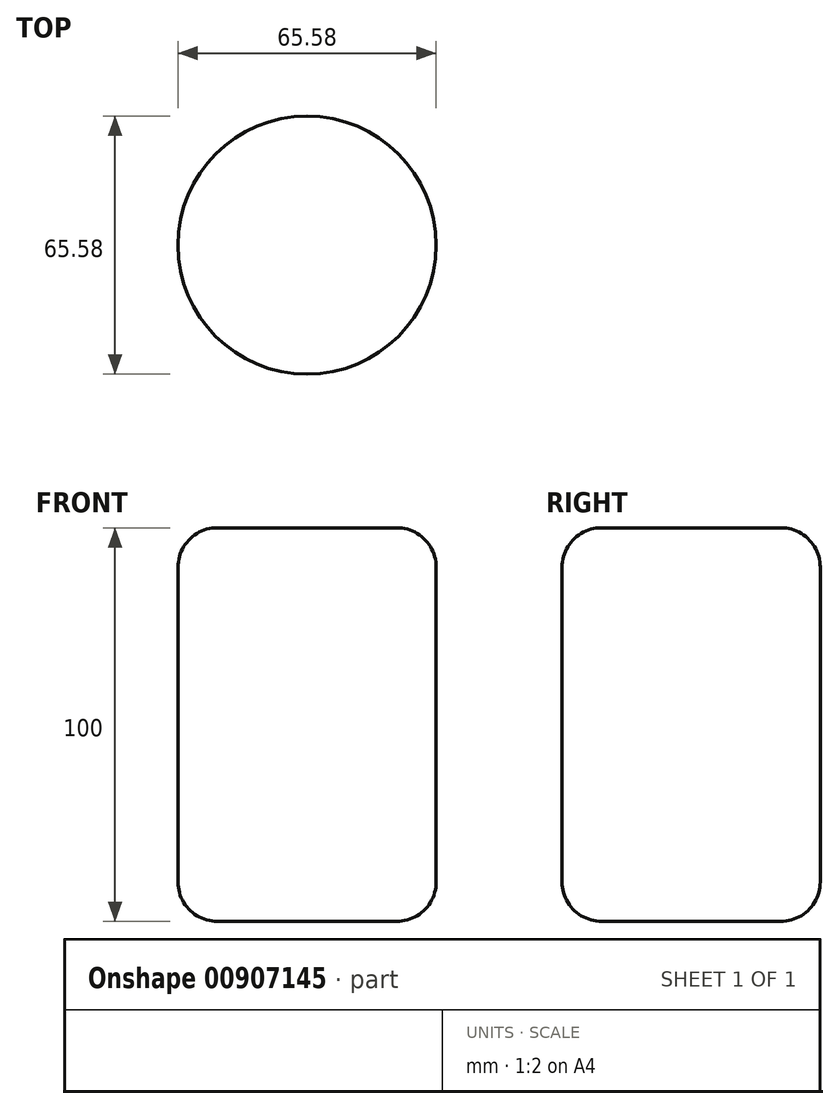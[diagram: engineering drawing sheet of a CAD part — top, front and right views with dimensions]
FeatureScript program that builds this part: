
annotation { "Feature Type Name" : "Feature", "Feature Type Description" : "" }
export const myFeature = defineFeature(function(context is Context, id is Id, definition is map)
    precondition{}
    {
        {
            var Q0;
            Q0=qCreatedBy(makeId("Top.planeOp"),FACE);
            var sketch = newSketch(context, id + "F0", { "sketchPlane" : qUnion([Q0])});
            skCircle(sketch, "E0", {"center": v(0, 0) * mm, "radius": 32.79 * mm});
            skSolve(sketch);
        }
        {
            var Q0;
            Q0 = qSketchRegion(id + "F0", true);
            extrude(context, id + "F1", {"entities" : qUnion([Q0]), "depth" : 100 * mm, "offsetDistance" : 25.4 * mm});
        }
        {
            var Q0;
            Q0=makeQuery(id+"F1.opExtrude","CAP_EDGE",EDGE,{"disambiguationData":[OSD([sQuery(id+"F0.wireOp",EDGE,"E0")])],"isStart":false});
            var Q1;
            Q1=makeQuery(id+"F1.opExtrude","CAP_EDGE",EDGE,{"disambiguationData":[OSD([sQuery(id+"F0.wireOp",EDGE,"E0")])],"isStart":true});
            fillet(context, id + "F2", {"entities" : qUnion([Q0, Q1]), "radius" : 10 * mm, "allowEdgeOverflow" : false});
        }
    });
